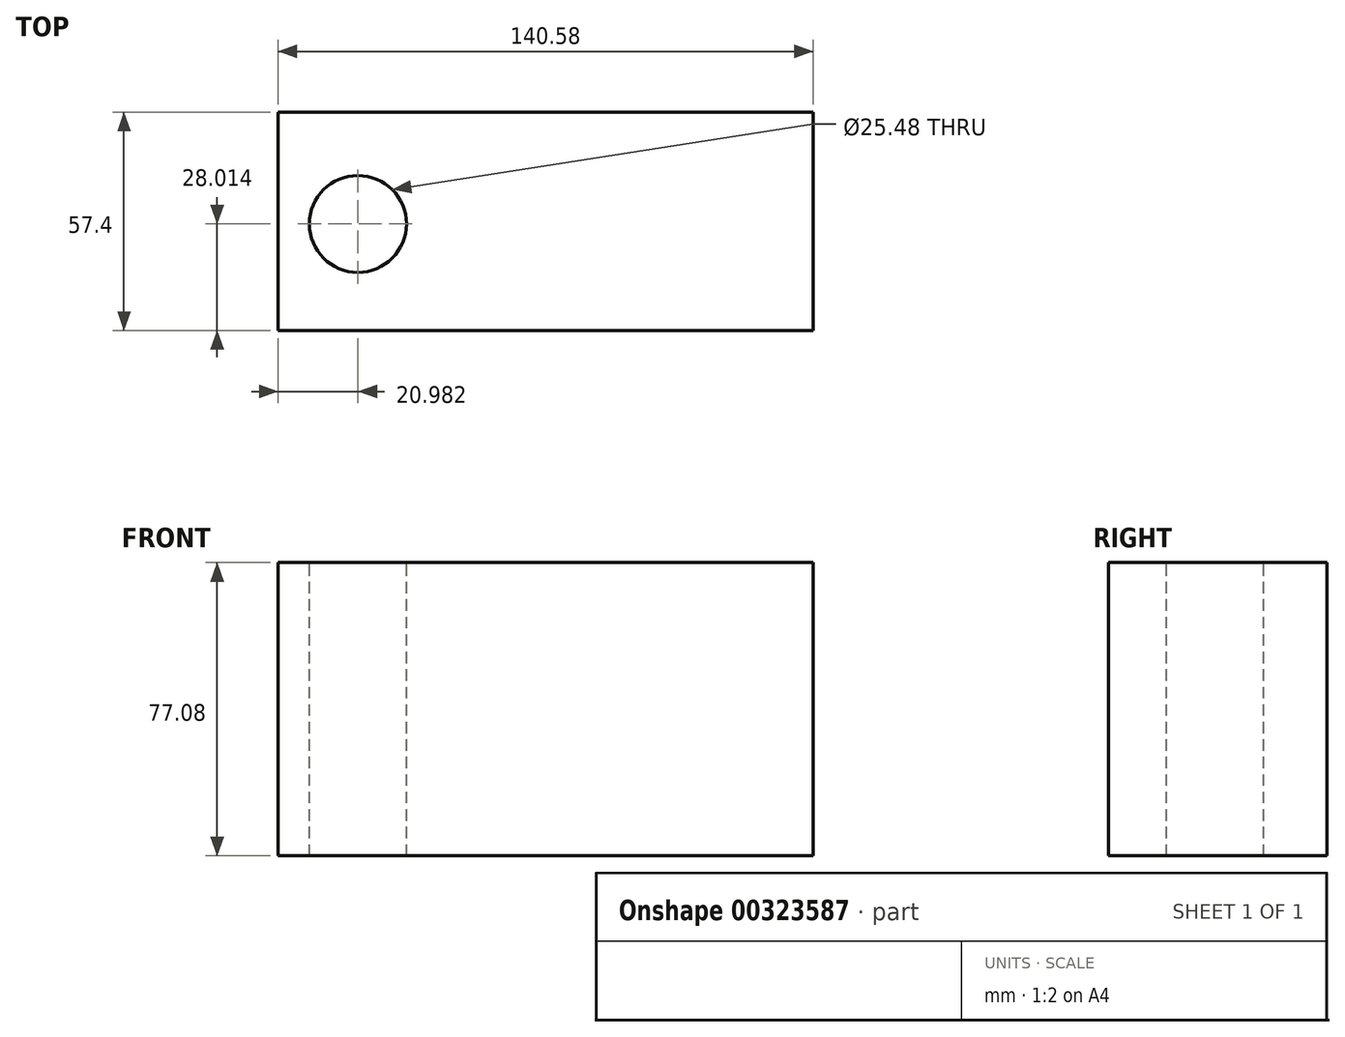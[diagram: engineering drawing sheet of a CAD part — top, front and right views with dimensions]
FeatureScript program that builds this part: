
annotation { "Feature Type Name" : "Feature", "Feature Type Description" : "" }
export const myFeature = defineFeature(function(context is Context, id is Id, definition is map)
    precondition{}
    {
        {
            var Q0;
            Q0=qCreatedBy(makeId("Front.planeOp"),FACE);
            var sketch = newSketch(context, id + "F0", { "sketchPlane" : qUnion([Q0])});
            skLineSegment(sketch, "E0.bottom", {"start": v(-70.46, 35.12) * mm, "end": v(70.12, 35.12) * mm});
            skLineSegment(sketch, "E0.top", {"start": v(-70.46, -41.96) * mm, "end": v(70.12, -41.96) * mm});
            skLineSegment(sketch, "E0.left", {"start": v(-70.46, 35.12) * mm, "end": v(-70.46, -41.96) * mm});
            skLineSegment(sketch, "E0.right", {"start": v(70.12, 35.12) * mm, "end": v(70.12, -41.96) * mm});
            skSolve(sketch);
        }
        {
            var Q0;
            Q0=makeQuery(id+"F0.imprint","IMPRINT",FACE,{"disambiguationData":[TD([[makeQuery(id+"F0.imprint","IMPRINT",EDGE,{"derivedFrom":sQuery(id+"F0.wireOp",EDGE,"E0.bottom")}),-1.0]])]});
            extrude(context, id + "F1", {"entities" : qUnion([Q0]), "depth" : 57.4 * mm});
        }
        {
            var Q0;
            Q0=makeQuery(id+"F1.opExtrude","SWEPT_FACE",FACE,{"disambiguationData":[OSD([sQuery(id+"F0.wireOp",EDGE,"E0.bottom")])]});
            var sketch = newSketch(context, id + "F2", { "sketchPlane" : qUnion([Q0])});
            skCircle(sketch, "E1", {"center": v(-49.48, -29.39) * mm, "radius": 12.74 * mm});
            skCircle(sketch, "E2", {"center": v(2.05, -29.39) * mm, "radius": 12.74 * mm});
            skSolve(sketch);
        }
        {
            var Q0;
            Q0=makeQuery(id+"F2.imprint","IMPRINT",FACE,{"disambiguationData":[TD([[makeQuery(id+"F2.imprint","IMPRINT",EDGE,{"derivedFrom":sQuery(id+"F2.wireOp",EDGE,"E1")}),1.0]])]});
            extrude(context, id + "F3", {"entities" : qUnion([Q0]), "operationType" : NewBodyOperationType.REMOVE, "oppositeDirection" : true, "depth" : 94.49 * mm});
        }
    });
